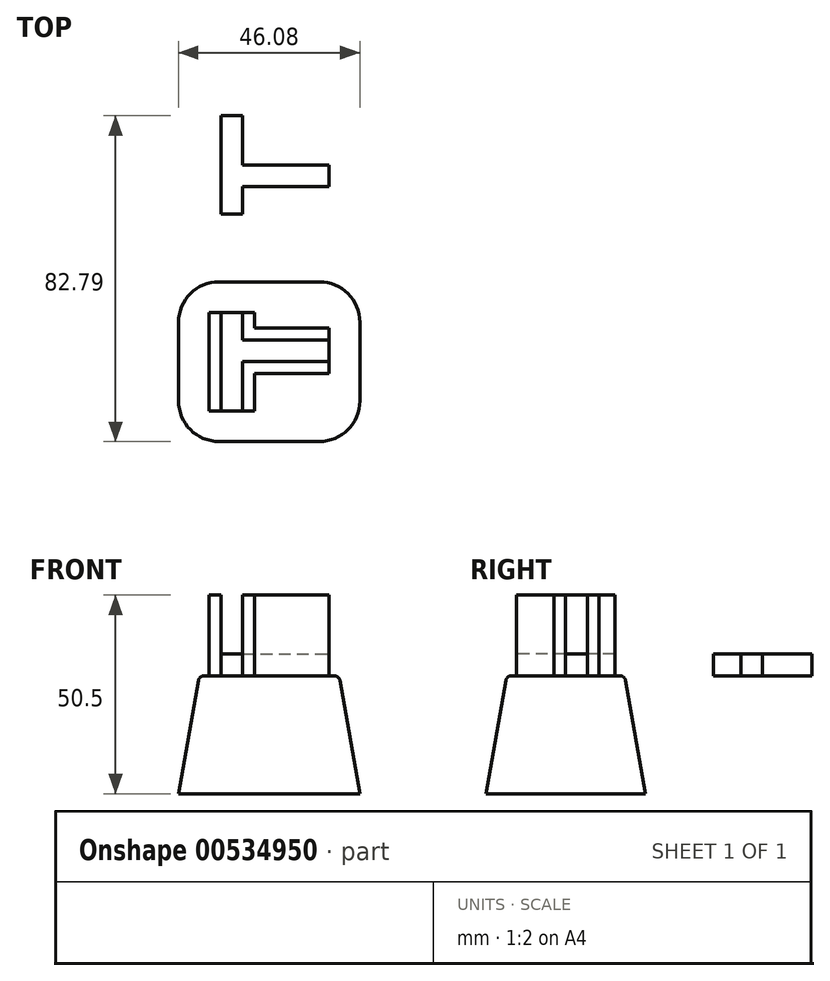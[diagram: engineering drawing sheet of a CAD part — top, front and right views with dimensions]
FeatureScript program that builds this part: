
annotation { "Feature Type Name" : "Feature", "Feature Type Description" : "" }
export const myFeature = defineFeature(function(context is Context, id is Id, definition is map)
    precondition{}
    {
        {
            var Q0;
            Q0=qCreatedBy(makeId("Top.planeOp"),FACE);
            var sketch = newSketch(context, id + "F0", { "sketchPlane" : qUnion([Q0])});
            skLineSegment(sketch, "E0.bottom", {"start": v(15.25, 12.5) * mm, "end": v(-15.25, 12.5) * mm});
            skLineSegment(sketch, "E0.top", {"start": v(15.25, -12.5) * mm, "end": v(-15.25, -12.5) * mm});
            skLineSegment(sketch, "E0.left", {"start": v(15.25, 12.5) * mm, "end": v(15.25, -12.5) * mm});
            skLineSegment(sketch, "E0.right", {"start": v(-15.25, 12.5) * mm, "end": v(-15.25, -12.5) * mm});
            skPoint(sketch, "E0.middle", {"position": v(0, 0) * mm});
            skLineSegment(sketch, "E1", {"start": v(-12.25, 12.5) * mm, "end": v(-12.25, -12.5) * mm});
            skLineSegment(sketch, "E2", {"start": v(-6.75, 12.5) * mm, "end": v(-6.75, 5.5) * mm});
            skLineSegment(sketch, "E3", {"start": v(-6.75, 5.5) * mm, "end": v(15.25, 5.5) * mm});
            skLineSegment(sketch, "E4", {"start": v(-6.75, 0) * mm, "end": v(15.25, 0) * mm});
            skLineSegment(sketch, "E5", {"start": v(-6.75, 5.5) * mm, "end": v(-6.75, 0) * mm, "construction": true});
            skLineSegment(sketch, "E6", {"start": v(-6.75, 0) * mm, "end": v(-6.75, -12.5) * mm});
            skLineSegment(sketch, "E7.0", {"start": v(-3.75, -3) * mm, "end": v(-3.75, -12.5) * mm});
            skLineSegment(sketch, "E7.1", {"start": v(-3.75, -3) * mm, "end": v(15.25, -3) * mm});
            skLineSegment(sketch, "E8.0", {"start": v(-3.75, 8.5) * mm, "end": v(15.25, 8.5) * mm});
            skLineSegment(sketch, "E8.1", {"start": v(-3.75, 12.5) * mm, "end": v(-3.75, 8.5) * mm});
            skLineSegment(sketch, "E9.bottom", {"start": v(12.75, -15) * mm, "end": v(-12.75, -15) * mm});
            skLineSegment(sketch, "E9.top", {"start": v(12.75, 15) * mm, "end": v(-12.75, 15) * mm});
            skLineSegment(sketch, "E9.left", {"start": v(17.75, -10) * mm, "end": v(17.75, 10) * mm});
            skLineSegment(sketch, "E9.right", {"start": v(-17.75, -10) * mm, "end": v(-17.75, 10) * mm});
            skPoint(sketch, "E10.visualSharp", {"position": v(-17.75, 15) * mm});
            skArc(sketch, "E10.filletArc", {"start": v(-12.75, 15) * mm, "mid": v(-16.29, 13.54) * mm, "end": v(-17.75, 10) * mm});
            skPoint(sketch, "E11.visualSharp", {"position": v(17.75, 15) * mm});
            skArc(sketch, "E11.filletArc", {"start": v(17.75, 10) * mm, "mid": v(16.29, 13.54) * mm, "end": v(12.75, 15) * mm});
            skPoint(sketch, "E12.visualSharp", {"position": v(17.75, -15) * mm});
            skArc(sketch, "E12.filletArc", {"start": v(12.75, -15) * mm, "mid": v(16.29, -13.54) * mm, "end": v(17.75, -10) * mm});
            skPoint(sketch, "E13.visualSharp", {"position": v(-17.75, -15) * mm});
            skArc(sketch, "E13.filletArc", {"start": v(-17.75, -10) * mm, "mid": v(-16.29, -13.54) * mm, "end": v(-12.75, -15) * mm});
            skSolve(sketch);
        }
        {
            var Q0;
            {var subQ0=sQuery(id+"F0.wireOp",EDGE,"E0.right");Q0=makeQuery(id+"F0.imprint","IMPRINT",FACE,{"disambiguationData":[TD([[makeQuery(id+"F0.imprint","IMPRINT",EDGE,{"derivedFrom":subQ0}),1.0]])]});}
            var Q1;
            {var subQ1=sQuery(id+"F0.wireOp",EDGE,"E4");Q1=makeQuery(id+"F0.imprint","IMPRINT",FACE,{"disambiguationData":[TD([[makeQuery(id+"F0.imprint","IMPRINT",EDGE,{"derivedFrom":subQ1}),-1.0]])]});}
            var Q2;
            {var subQ0=sQuery(id+"F0.wireOp",EDGE,"E2");Q2=makeQuery(id+"F0.imprint","IMPRINT",FACE,{"disambiguationData":[TD([[makeQuery(id+"F0.imprint","IMPRINT",EDGE,{"derivedFrom":subQ0}),1.0]])]});}
            extrude(context, id + "F1", {"entities" : qUnion([Q0, Q1, Q2]), "depth" : 20.5 * mm, "offsetDistance" : 25 * mm});
        }
        {
            var Q0;
            {var subQ0=sQuery(id+"F0.wireOp",EDGE,"E1");Q0=makeQuery(id+"F0.imprint","IMPRINT",FACE,{"disambiguationData":[TD([[makeQuery(id+"F0.imprint","IMPRINT",EDGE,{"derivedFrom":subQ0}),1.0]])]});}
            extrude(context, id + "F2", {"entities" : qUnion([Q0]), "depth" : 5.5 * mm, "offsetDistance" : 25 * mm});
        }
        {
            var Q0;
            Q0 = qSketchRegion(id + "F0", true);
            var Q1;
            {var subQ0=sQuery(id+"F0.wireOp",EDGE,"E0.right");Q1=makeQuery(id+"F0.imprint","IMPRINT",FACE,{"disambiguationData":[TD([[makeQuery(id+"F0.imprint","IMPRINT",EDGE,{"derivedFrom":subQ0}),1.0]])]});}
            var Q2;
            {var subQ0=sQuery(id+"F0.wireOp",EDGE,"E1");Q2=makeQuery(id+"F0.imprint","IMPRINT",FACE,{"disambiguationData":[TD([[makeQuery(id+"F0.imprint","IMPRINT",EDGE,{"derivedFrom":subQ0}),1.0]])]});}
            var Q3;
            {var subQ1=sQuery(id+"F0.wireOp",EDGE,"E4");Q3=makeQuery(id+"F0.imprint","IMPRINT",FACE,{"disambiguationData":[TD([[makeQuery(id+"F0.imprint","IMPRINT",EDGE,{"derivedFrom":subQ1}),-1.0]])]});}
            var Q4;
            {var subQ0=sQuery(id+"F0.wireOp",EDGE,"E2");Q4=makeQuery(id+"F0.imprint","IMPRINT",FACE,{"disambiguationData":[TD([[makeQuery(id+"F0.imprint","IMPRINT",EDGE,{"derivedFrom":subQ0}),1.0]])]});}
            var Q5;
            {var subQ4=sQuery(id+"F0.wireOp",EDGE,"E8.0");Q5=makeQuery(id+"F0.imprint","IMPRINT",FACE,{"disambiguationData":[TD([[makeQuery(id+"F0.imprint","IMPRINT",EDGE,{"derivedFrom":subQ4}),1.0]])]});}
            var Q6;
            {var subQ3=sQuery(id+"F0.wireOp",EDGE,"E7.0");Q6=makeQuery(id+"F0.imprint","IMPRINT",FACE,{"disambiguationData":[TD([[makeQuery(id+"F0.imprint","IMPRINT",EDGE,{"derivedFrom":subQ3}),1.0]])]});}
            extrude(context, id + "F3", {"entities" : qUnion([Q0, Q1, Q2, Q3, Q4, Q5, Q6]), "oppositeDirection" : true, "depth" : 30 * mm, "offsetDistance" : 25 * mm, "hasDraft" : true, "draftAngle" : 10 * degree});
        }
        {
            var Q0;
            Q0=makeQuery(id+"F3.opExtrude","CAP_EDGE",EDGE,{"disambiguationData":[OSD([sQuery(id+"F0.wireOp",EDGE,"E9.right")])],"isStart":true});
            var Q1;
            Q1=makeQuery(id+"F3.opExtrude","CAP_EDGE",EDGE,{"disambiguationData":[OSD([sQuery(id+"F0.wireOp",EDGE,"E13.filletArc")])],"isStart":true});
            var Q2;
            Q2=makeQuery(id+"F3.opExtrude","CAP_EDGE",EDGE,{"disambiguationData":[OSD([sQuery(id+"F0.wireOp",EDGE,"E10.filletArc")])],"isStart":true});
            var Q3;
            Q3=makeQuery(id+"F3.opExtrude","CAP_EDGE",EDGE,{"disambiguationData":[OSD([sQuery(id+"F0.wireOp",EDGE,"E9.top")])],"isStart":true});
            var Q4;
            Q4=makeQuery(id+"F3.opExtrude","CAP_EDGE",EDGE,{"disambiguationData":[OSD([sQuery(id+"F0.wireOp",EDGE,"E11.filletArc")])],"isStart":true});
            var Q5;
            Q5=makeQuery(id+"F3.opExtrude","CAP_EDGE",EDGE,{"disambiguationData":[OSD([sQuery(id+"F0.wireOp",EDGE,"E9.left")])],"isStart":true});
            var Q6;
            Q6=makeQuery(id+"F3.opExtrude","CAP_EDGE",EDGE,{"disambiguationData":[OSD([sQuery(id+"F0.wireOp",EDGE,"E9.bottom")])],"isStart":true});
            var Q7;
            Q7=makeQuery(id+"F3.opExtrude","CAP_EDGE",EDGE,{"disambiguationData":[OSD([sQuery(id+"F0.wireOp",EDGE,"E12.filletArc")])],"isStart":true});
            fillet(context, id + "F4", {"entities" : qUnion([Q0, Q1, Q2, Q3, Q4, Q5, Q6, Q7]), "radius" : 1.5 * mm, "tangentPropagation" : true, "allowEdgeOverflow" : false});
        }
        {
            var Q0;
            Q0=qCreatedBy(makeId("Front.planeOp"),FACE);
            cPlane(context, id + "F5", {"entities" : qUnion([Q0]), "cplaneType" : CPlaneType.OFFSET, "offset" : 25 * mm, "oppositeDirection" : true, "width" : 150 * mm, "height" : 150 * mm});
        }
        {
            var Q0;
            Q0=makeQuery(id+"F2.opExtrude","SWEPT_BODY",BODY,{"disambiguationData":[OSD([sQuery(id+"F0.wireOp",EDGE,"E0.bottom"),sQuery(id+"F0.wireOp",EDGE,"E0.top"),sQuery(id+"F0.wireOp",EDGE,"E0.left"),sQuery(id+"F0.wireOp",EDGE,"E1"),sQuery(id+"F0.wireOp",EDGE,"E2"),sQuery(id+"F0.wireOp",EDGE,"E3"),sQuery(id+"F0.wireOp",EDGE,"E4"),sQuery(id+"F0.wireOp",EDGE,"E6")])]});
            var Q1;
            Q1=qCreatedBy(id+"F5.planeOp",FACE);
            mirror(context, id + "F6", {"entities" : qUnion([Q0]), "mirrorPlane" : qUnion([Q1])});
        }
    });
